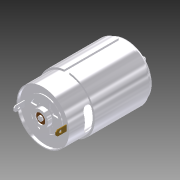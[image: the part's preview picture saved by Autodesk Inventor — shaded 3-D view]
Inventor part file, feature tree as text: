
AUTODESK INVENTOR PART (.ipt)
format: ipt  version: 2012 (Build 160160000, 160)  size: 303,616 bytes
history: native  units: in
note: dims shown in document units (in); Inventor stores cm internally (conversion verified against a paired STEP export)
features: sketch x15, other x3, plane x3
ambient origin geometry x8: Origin, YZ Plane, XZ Plane, XY Plane, X Axis, Y Axis, Z Axis, Center Point
bodies: Solid1 (feature_tree)
feature tree (21):
  other  "MabuchiRS550.ipt"
  other  "Solid1::MabuchiRS550.ipt"
  sketch  "Sketch1"  dims[d0=0.3937in]
  sketch  "Sketch2"
  sketch  "Sketch3"
  sketch  "Sketch4"
  sketch  "Sketch5"
  sketch  "Sketch6"
  sketch  "Sketch7"
  sketch  "Sketch8"
  sketch  "Sketch9"
  sketch  "Sketch10"
  sketch  "Sketch11"
  sketch  "Sketch12"
  sketch  "Sketch13"
  sketch  "Sketch14"
  sketch  "Sketch15"
  plane  "Work Plane1"
  plane  "Work Plane2"
  plane  "Work Plane3"
  other  "TaggingFeature1"
